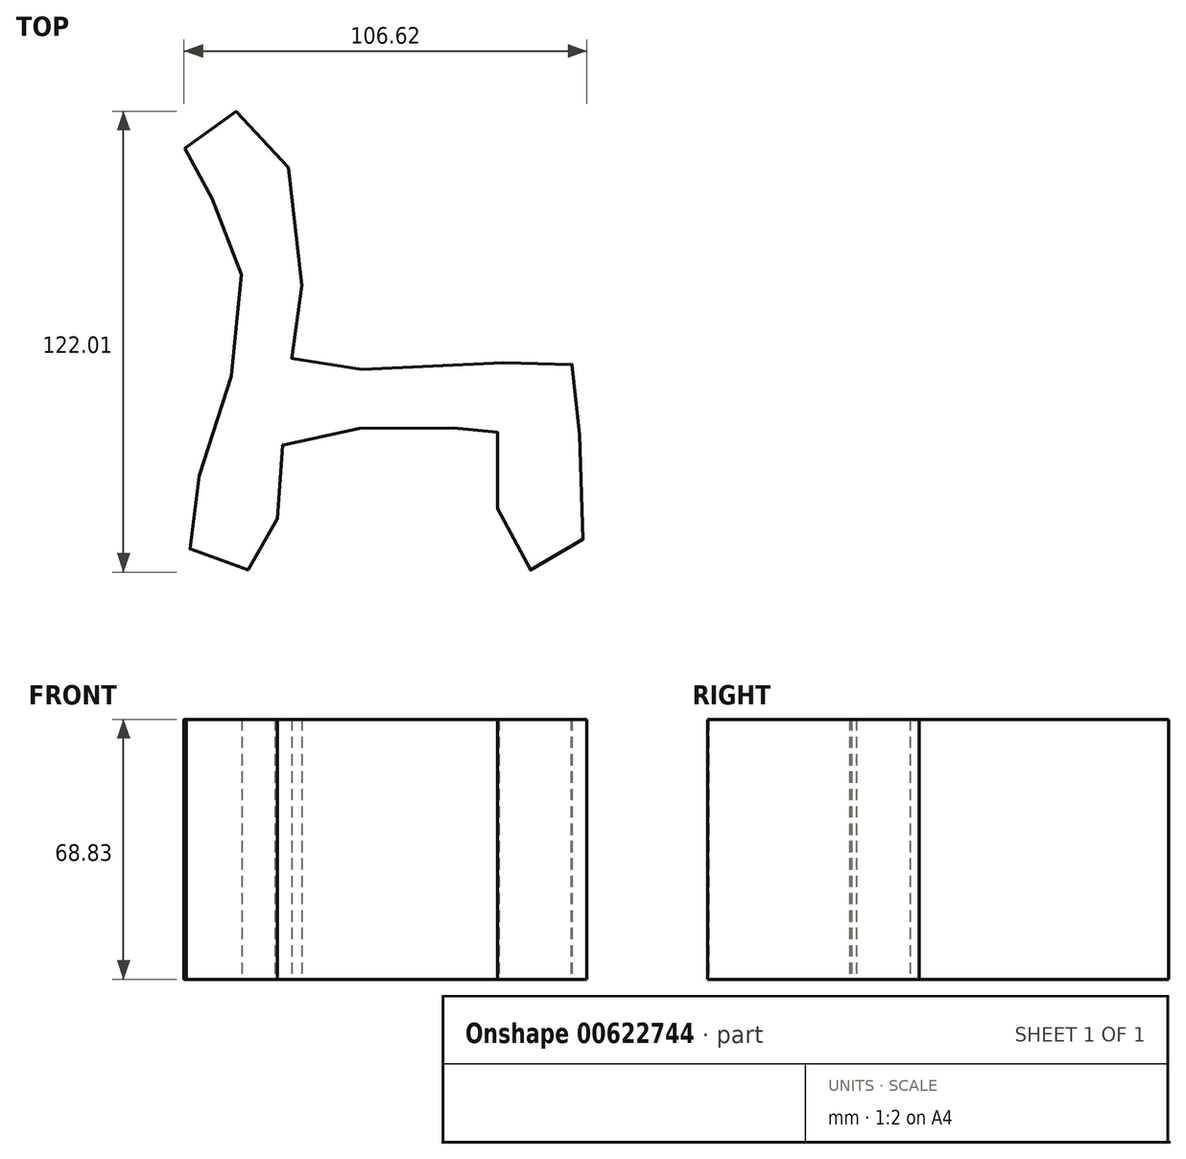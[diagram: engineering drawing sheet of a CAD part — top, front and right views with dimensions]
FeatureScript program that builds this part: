
annotation { "Feature Type Name" : "Feature", "Feature Type Description" : "" }
export const myFeature = defineFeature(function(context is Context, id is Id, definition is map)
    precondition{}
    {
        {
            var Q0;
            Q0=qCreatedBy(makeId("Top.planeOp"),FACE);
            var sketch = newSketch(context, id + "F0", { "sketchPlane" : qUnion([Q0])});
            skFitSpline(sketch, "E0", {"points": [v(-61.67, 43.33) * mm, v(-50.43, 24.1) * mm, v(-52.5, -28.54) * mm, v(-59.01, -64.63) * mm, v(-38.9, -64.93) * mm, v(-35.94, -35.64) * mm, v(5.77, -31.2) * mm, v(20.85, -31.2) * mm, v(23.81, -63.74) * mm, v(42.15, -64.34) * mm, v(40.67, -15.83) * mm, v(40.08, -13.16) * mm, v(-31.2, -14.35) * mm, v(-31.8, -5.18) * mm, v(-42.74, 51.91) * mm, v(-61.67, 43.33) * mm]});
            skSolve(sketch);
        }
        {
            var Q0;
            Q0=makeQuery(id+"F0.imprint","IMPRINT",FACE,{"disambiguationData":[TD([[makeQuery(id+"F0.imprint","IMPRINT",EDGE,{"derivedFrom":sQuery(id+"F0.wireOp",EDGE,"E0")}),1.0]])]});
            extrude(context, id + "F1", {"entities" : qUnion([Q0]), "depth" : 68.83 * mm, "offsetDistance" : 25.4 * mm});
        }
        {
            var Q0;
            Q0=makeQuery(id+"F1.opExtrude","CAP_FACE",FACE,{"disambiguationData":[OSD([sQuery(id+"F0.wireOp",EDGE,"E0")])],"isStart":true});
            var sketch = newSketch(context, id + "F2", { "sketchPlane" : qUnion([Q0])});
            skSolve(sketch);
        }
    });
